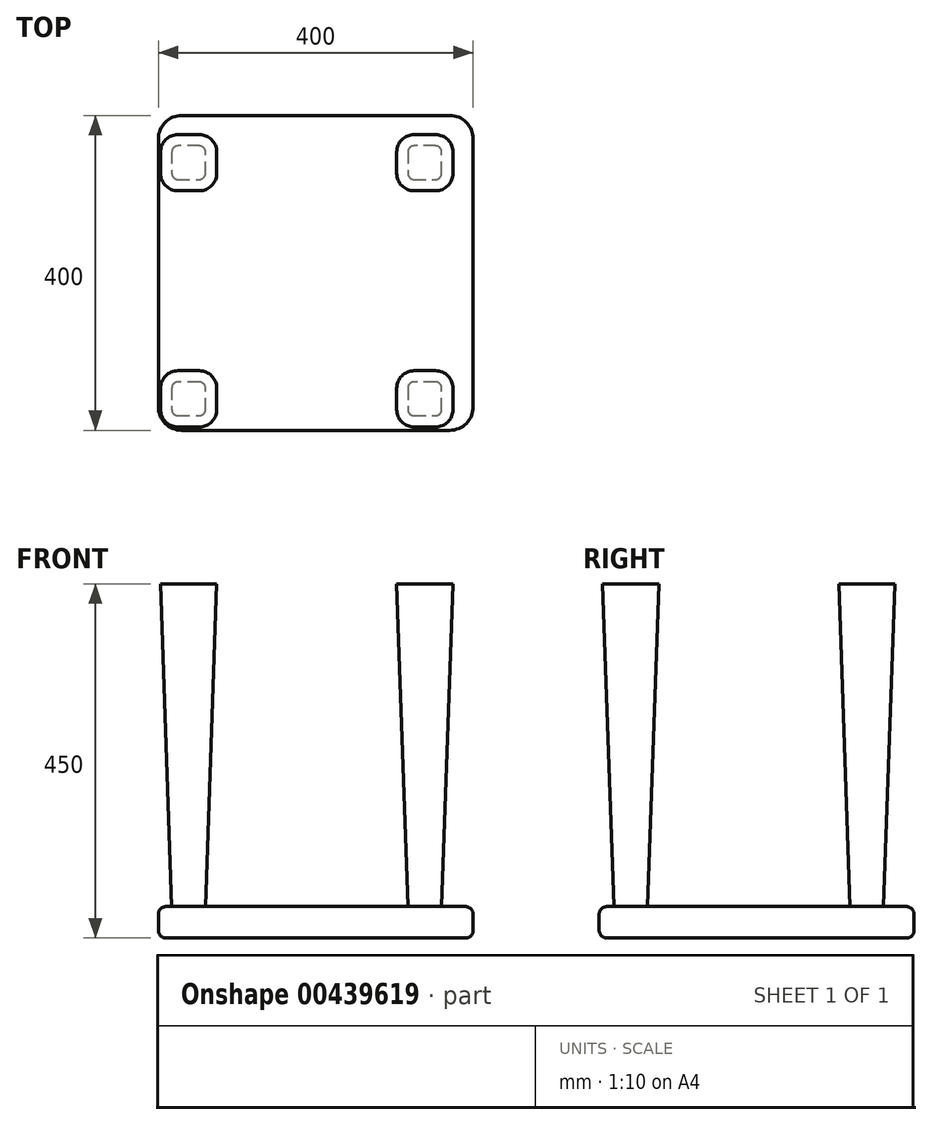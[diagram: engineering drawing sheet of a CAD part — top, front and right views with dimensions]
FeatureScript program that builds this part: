
annotation { "Feature Type Name" : "Feature", "Feature Type Description" : "" }
export const myFeature = defineFeature(function(context is Context, id is Id, definition is map)
    precondition{}
    {
        {
            var Q0;
            Q0=qCreatedBy(makeId("Top.planeOp"),FACE);
            var sketch = newSketch(context, id + "F0", { "sketchPlane" : qUnion([Q0])});
            skLineSegment(sketch, "E0.bottom", {"start": v(170, 200) * mm, "end": v(-170, 200) * mm});
            skLineSegment(sketch, "E0.top", {"start": v(170, -200) * mm, "end": v(-170, -200) * mm});
            skLineSegment(sketch, "E0.left", {"start": v(200, 170) * mm, "end": v(200, -170) * mm});
            skLineSegment(sketch, "E0.right", {"start": v(-200, 170) * mm, "end": v(-200, -170) * mm});
            skPoint(sketch, "E0.middle", {"position": v(0, 0) * mm});
            skPoint(sketch, "E1.visualSharp", {"position": v(-200, 200) * mm});
            skArc(sketch, "E1.filletArc", {"start": v(-170, 200) * mm, "mid": v(-191.21, 191.21) * mm, "end": v(-200, 170) * mm});
            skPoint(sketch, "E2.visualSharp", {"position": v(200, 200) * mm});
            skArc(sketch, "E2.filletArc", {"start": v(200, 170) * mm, "mid": v(191.21, 191.21) * mm, "end": v(170, 200) * mm});
            skPoint(sketch, "E3.visualSharp", {"position": v(200, -200) * mm});
            skArc(sketch, "E3.filletArc", {"start": v(170, -200) * mm, "mid": v(191.21, -191.21) * mm, "end": v(200, -170) * mm});
            skPoint(sketch, "E4.visualSharp", {"position": v(-200, -200) * mm});
            skArc(sketch, "E4.filletArc", {"start": v(-200, -170) * mm, "mid": v(-191.21, -191.21) * mm, "end": v(-170, -200) * mm});
            skSolve(sketch);
        }
        {
            var Q0;
            Q0=makeQuery(id+"F0.imprint","IMPRINT",FACE,{"disambiguationData":[TD([[makeQuery(id+"F0.imprint","IMPRINT",EDGE,{"derivedFrom":sQuery(id+"F0.wireOp",EDGE,"E0.bottom")}),1.0]])]});
            var sketch = newSketch(context, id + "F1", { "sketchPlane" : qUnion([Q0])});
            skLineSegment(sketch, "E5.bottom", {"start": v(-147.83, 120) * mm, "end": v(-175.13, 120) * mm});
            skLineSegment(sketch, "E5.top", {"start": v(-147.83, 160) * mm, "end": v(-175.13, 160) * mm});
            skLineSegment(sketch, "E5.left", {"start": v(-141.48, 126.35) * mm, "end": v(-141.48, 153.65) * mm});
            skLineSegment(sketch, "E5.right", {"start": v(-181.48, 126.35) * mm, "end": v(-181.48, 153.65) * mm});
            skPoint(sketch, "E5.middle", {"position": v(-161.48, 140) * mm});
            skPoint(sketch, "E6.visualSharp", {"position": v(-141.48, 160) * mm});
            skArc(sketch, "E6.filletArc", {"start": v(-141.48, 153.65) * mm, "mid": v(-143.34, 158.14) * mm, "end": v(-147.83, 160) * mm});
            skPoint(sketch, "E7.visualSharp", {"position": v(-141.48, 120) * mm});
            skArc(sketch, "E7.filletArc", {"start": v(-147.83, 120) * mm, "mid": v(-143.34, 121.86) * mm, "end": v(-141.48, 126.35) * mm});
            skPoint(sketch, "E8.visualSharp", {"position": v(-181.48, 120) * mm});
            skArc(sketch, "E8.filletArc", {"start": v(-181.48, 126.35) * mm, "mid": v(-179.62, 121.86) * mm, "end": v(-175.13, 120) * mm});
            skPoint(sketch, "E9.visualSharp", {"position": v(-181.48, 160) * mm});
            skArc(sketch, "E9.filletArc", {"start": v(-175.13, 160) * mm, "mid": v(-179.62, 158.14) * mm, "end": v(-181.48, 153.65) * mm});
            skLineSegment(sketch, "E10.0.1.0", {"start": v(-181.48, -173.65) * mm, "end": v(-181.48, -146.35) * mm});
            skLineSegment(sketch, "E10.0.1.1", {"start": v(-141.48, -173.65) * mm, "end": v(-141.48, -146.35) * mm});
            skLineSegment(sketch, "E10.0.1.2", {"start": v(-147.83, -140) * mm, "end": v(-175.13, -140) * mm});
            skPoint(sketch, "E10.0.1.3", {"position": v(-161.48, -160) * mm});
            skPoint(sketch, "E10.0.1.4", {"position": v(-141.48, -140) * mm});
            skPoint(sketch, "E10.0.1.5", {"position": v(-141.48, -180) * mm});
            skPoint(sketch, "E10.0.1.6", {"position": v(-181.48, -180) * mm});
            skPoint(sketch, "E10.0.1.7", {"position": v(-181.48, -140) * mm});
            skLineSegment(sketch, "E10.0.1.8", {"start": v(-147.83, -180) * mm, "end": v(-175.13, -180) * mm});
            skArc(sketch, "E10.0.1.9", {"start": v(-175.13, -140) * mm, "mid": v(-179.62, -141.86) * mm, "end": v(-181.48, -146.35) * mm});
            skArc(sketch, "E10.0.1.10", {"start": v(-181.48, -173.65) * mm, "mid": v(-179.62, -178.14) * mm, "end": v(-175.13, -180) * mm});
            skArc(sketch, "E10.0.1.11", {"start": v(-147.83, -180) * mm, "mid": v(-143.34, -178.14) * mm, "end": v(-141.48, -173.65) * mm});
            skArc(sketch, "E10.0.1.12", {"start": v(-141.48, -146.35) * mm, "mid": v(-143.34, -141.86) * mm, "end": v(-147.83, -140) * mm});
            skLineSegment(sketch, "E10.1.0.0", {"start": v(118.52, 126.35) * mm, "end": v(118.52, 153.65) * mm});
            skLineSegment(sketch, "E10.1.0.1", {"start": v(158.52, 126.35) * mm, "end": v(158.52, 153.65) * mm});
            skLineSegment(sketch, "E10.1.0.2", {"start": v(152.17, 160) * mm, "end": v(124.87, 160) * mm});
            skPoint(sketch, "E10.1.0.3", {"position": v(138.52, 140) * mm});
            skPoint(sketch, "E10.1.0.4", {"position": v(158.52, 160) * mm});
            skPoint(sketch, "E10.1.0.5", {"position": v(158.52, 120) * mm});
            skPoint(sketch, "E10.1.0.6", {"position": v(118.52, 120) * mm});
            skPoint(sketch, "E10.1.0.7", {"position": v(118.52, 160) * mm});
            skLineSegment(sketch, "E10.1.0.8", {"start": v(152.17, 120) * mm, "end": v(124.87, 120) * mm});
            skArc(sketch, "E10.1.0.9", {"start": v(124.87, 160) * mm, "mid": v(120.38, 158.14) * mm, "end": v(118.52, 153.65) * mm});
            skArc(sketch, "E10.1.0.10", {"start": v(118.52, 126.35) * mm, "mid": v(120.38, 121.86) * mm, "end": v(124.87, 120) * mm});
            skArc(sketch, "E10.1.0.11", {"start": v(152.17, 120) * mm, "mid": v(156.66, 121.86) * mm, "end": v(158.52, 126.35) * mm});
            skArc(sketch, "E10.1.0.12", {"start": v(158.52, 153.65) * mm, "mid": v(156.66, 158.14) * mm, "end": v(152.17, 160) * mm});
            skLineSegment(sketch, "E10.1.1.0", {"start": v(118.52, -173.65) * mm, "end": v(118.52, -146.35) * mm});
            skLineSegment(sketch, "E10.1.1.1", {"start": v(158.52, -173.65) * mm, "end": v(158.52, -146.35) * mm});
            skLineSegment(sketch, "E10.1.1.2", {"start": v(152.17, -140) * mm, "end": v(124.87, -140) * mm});
            skPoint(sketch, "E10.1.1.3", {"position": v(138.52, -160) * mm});
            skPoint(sketch, "E10.1.1.4", {"position": v(158.52, -140) * mm});
            skPoint(sketch, "E10.1.1.5", {"position": v(158.52, -180) * mm});
            skPoint(sketch, "E10.1.1.6", {"position": v(118.52, -180) * mm});
            skPoint(sketch, "E10.1.1.7", {"position": v(118.52, -140) * mm});
            skLineSegment(sketch, "E10.1.1.8", {"start": v(152.17, -180) * mm, "end": v(124.87, -180) * mm});
            skArc(sketch, "E10.1.1.9", {"start": v(124.87, -140) * mm, "mid": v(120.38, -141.86) * mm, "end": v(118.52, -146.35) * mm});
            skArc(sketch, "E10.1.1.10", {"start": v(118.52, -173.65) * mm, "mid": v(120.38, -178.14) * mm, "end": v(124.87, -180) * mm});
            skArc(sketch, "E10.1.1.11", {"start": v(152.17, -180) * mm, "mid": v(156.66, -178.14) * mm, "end": v(158.52, -173.65) * mm});
            skArc(sketch, "E10.1.1.12", {"start": v(158.52, -146.35) * mm, "mid": v(156.66, -141.86) * mm, "end": v(152.17, -140) * mm});
            skLineSegment(sketch, "E10.direction1", {"start": v(-181.48, 120) * mm, "end": v(118.52, 120) * mm, "construction": true});
            skLineSegment(sketch, "E10.direction2", {"start": v(-181.48, 120) * mm, "end": v(-181.48, -180) * mm, "construction": true});
            skSolve(sketch);
        }
        {
            var Q0;
            Q0 = qSketchRegion(id + "F0", true);
            extrude(context, id + "F2", {"entities" : qUnion([Q0]), "depth" : 40 * mm});
        }
        {
            var Q0;
            Q0 = qSketchRegion(id + "F1", true);
            extrude(context, id + "F3", {"entities" : qUnion([Q0]), "operationType" : NewBodyOperationType.ADD, "depth" : 450 * mm, "hasDraft" : true, "draftAngle" : 2 * degree});
        }
        {
            var Q0;
            Q0=makeQuery(id+"F2.opExtrude","SWEPT_FACE",FACE,{"disambiguationData":[OSD([sQuery(id+"F0.wireOp",EDGE,"E2.filletArc")])]});
            fillet(context, id + "F4", {"entities" : qUnion([Q0]), "radius" : 10 * mm, "tangentPropagation" : true, "allowEdgeOverflow" : false});
        }
    });
